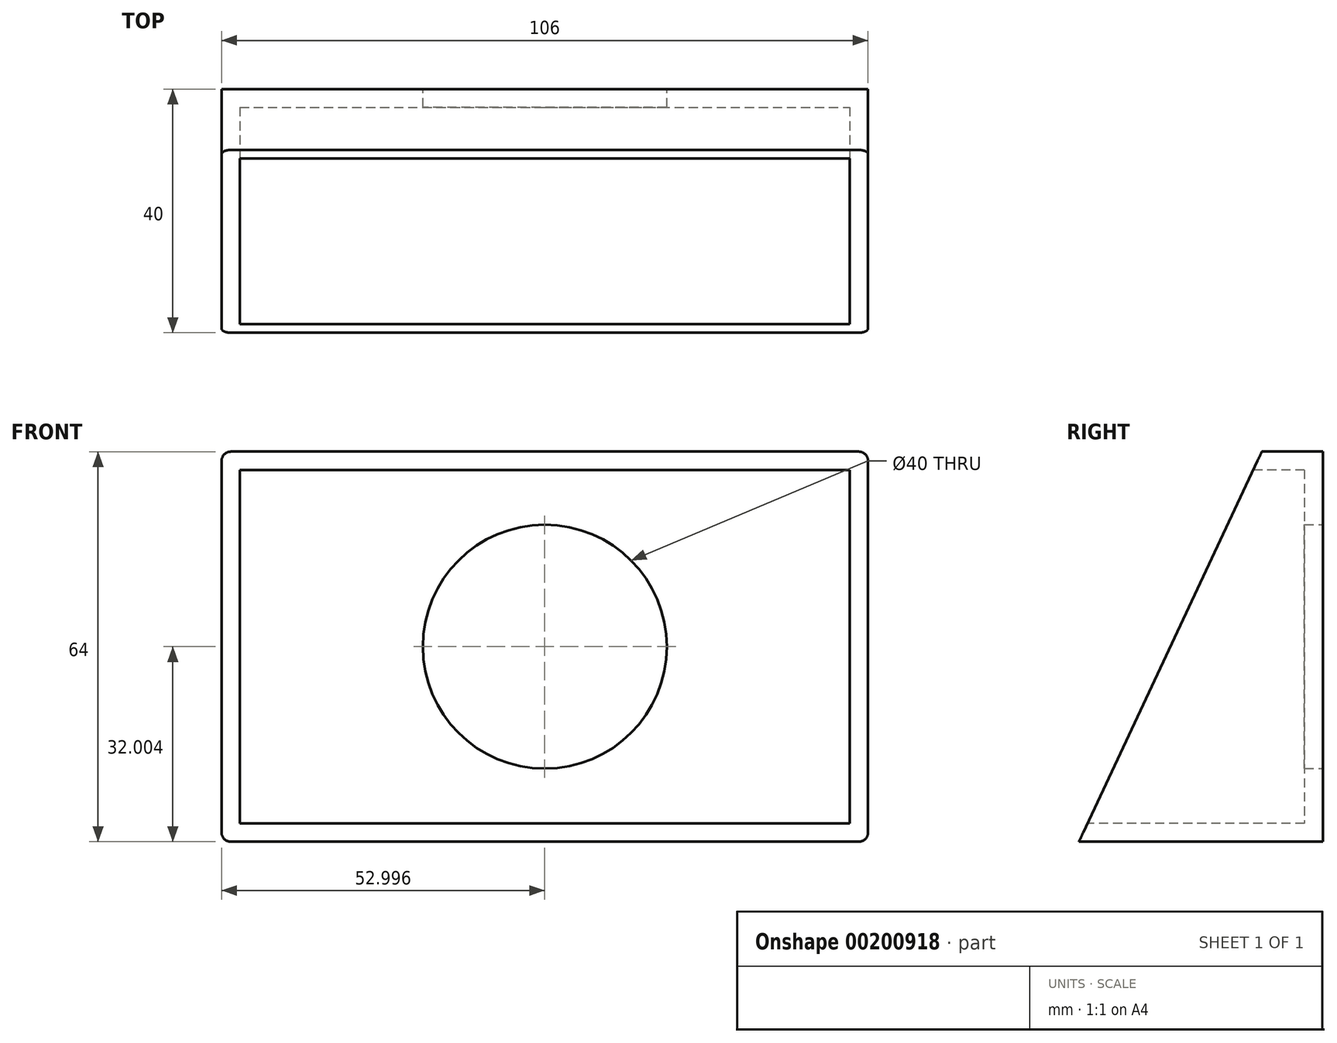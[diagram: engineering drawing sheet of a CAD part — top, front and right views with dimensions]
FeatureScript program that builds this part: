
annotation { "Feature Type Name" : "Feature", "Feature Type Description" : "" }
export const myFeature = defineFeature(function(context is Context, id is Id, definition is map)
    precondition{}
    {
        {
            var Q0;
            Q0=qCreatedBy(makeId("Front.planeOp"),FACE);
            var sketch = newSketch(context, id + "F0", { "sketchPlane" : qUnion([Q0])});
            skCircle(sketch, "E0", {"center": v(0, 0) * mm, "radius": 20 * mm});
            skLineSegment(sketch, "E1.bottom", {"start": v(-53, 32) * mm, "end": v(53, 32) * mm});
            skLineSegment(sketch, "E1.top", {"start": v(-53, -32) * mm, "end": v(53, -32) * mm});
            skLineSegment(sketch, "E1.left", {"start": v(-53, 32) * mm, "end": v(-53, -32) * mm});
            skLineSegment(sketch, "E1.right", {"start": v(53, 32) * mm, "end": v(53, -32) * mm});
            skSolve(sketch);
        }
        {
            var Q0;
            Q0=makeQuery(id+"F0.imprint","IMPRINT",FACE,{"disambiguationData":[TD([[makeQuery(id+"F0.imprint","IMPRINT",EDGE,{"derivedFrom":sQuery(id+"F0.wireOp",EDGE,"E0")}),-1.0]])]});
            extrude(context, id + "F1", {"entities" : qUnion([Q0]), "depth" : 40 * mm});
        }
        {
            var Q0;
            Q0=makeQuery(id+"F1.opExtrude","SWEPT_FACE",FACE,{"disambiguationData":[OSD([sQuery(id+"F0.wireOp",EDGE,"E1.right")])]});
            var sketch = newSketch(context, id + "F2", { "sketchPlane" : qUnion([Q0])});
            skLineSegment(sketch, "E2.0", {"start": v(-40, -32) * mm, "end": v(0, -32) * mm});
            skPoint(sketch, "E3.0", {"position": v(-40, 0) * mm});
            skPoint(sketch, "E4.0", {"position": v(-40, 32) * mm});
            skLineSegment(sketch, "E5", {"start": v(-40, 32) * mm, "end": v(-40, -32) * mm});
            skLineSegment(sketch, "E6.0", {"start": v(-40, 32) * mm, "end": v(0, 32) * mm});
            skLineSegment(sketch, "E7.0", {"start": v(0, 32) * mm, "end": v(0, -32) * mm});
            skLineSegment(sketch, "E8", {"start": v(0, 32) * mm, "end": v(-10, 32) * mm});
            skLineSegment(sketch, "E9", {"start": v(-10, 32) * mm, "end": v(-40, -32) * mm});
            skLineSegment(sketch, "E10", {"start": v(0, -32) * mm, "end": v(0, 32) * mm});
            skSolve(sketch);
        }
        {
            var Q0;
            Q0=makeQuery(id+"F2.imprint","IMPRINT",FACE,{"disambiguationData":[TD([[makeQuery(id+"F2.imprint","IMPRINT",EDGE,{"derivedFrom":sQuery(id+"F2.wireOp",EDGE,"E5")}),1.0]])]});
            extrude(context, id + "F3", {"entities" : qUnion([Q0]), "operationType" : NewBodyOperationType.REMOVE, "oppositeDirection" : true, "depth" : 120 * mm});
        }
        {
            var Q0;
            Q0=makeQuery(id+"F1.opExtrude","SWEPT_EDGE",EDGE,{"disambiguationData":[OSD([sQuery(id+"F0.wireOp",EDGE,"E1.bottom"),sQuery(id+"F0.wireOp",EDGE,"E1.right")])]});
            var Q1;
            Q1=makeQuery(id+"F1.opExtrude","SWEPT_EDGE",EDGE,{"disambiguationData":[OSD([sQuery(id+"F0.wireOp",EDGE,"E1.bottom"),sQuery(id+"F0.wireOp",EDGE,"E1.left")])]});
            var Q2;
            Q2=makeQuery(id+"F1.opExtrude","SWEPT_EDGE",EDGE,{"disambiguationData":[OSD([sQuery(id+"F0.wireOp",EDGE,"E1.top"),sQuery(id+"F0.wireOp",EDGE,"E1.left")])]});
            var Q3;
            Q3=makeQuery(id+"F1.opExtrude","SWEPT_EDGE",EDGE,{"disambiguationData":[OSD([sQuery(id+"F0.wireOp",EDGE,"E1.top"),sQuery(id+"F0.wireOp",EDGE,"E1.right")])]});
            fillet(context, id + "F4", {"entities" : qUnion([Q0, Q1, Q2, Q3]), "radius" : 1.5 * mm, "tangentPropagation" : true, "allowEdgeOverflow" : false});
        }
        {
            var Q0;
            Q0=makeQuery(id+"F3.boolean.opBoolean","COPY",FACE,{"derivedFrom":makeQuery(id+"F3.opExtrude","SWEPT_FACE",FACE,{"disambiguationData":[OSD([sQuery(id+"F2.wireOp",EDGE,"E9")])]})});
            var Q1;
            Q1=makeQuery(id+"F1.opExtrude","SWEPT_FACE",FACE,{"disambiguationData":[OSD([sQuery(id+"F0.wireOp",EDGE,"E0")])]});
            shell(context, id + "F5", {"entities" : qUnion([Q0, Q1]), "thickness" : 3 * mm});
        }
    });
